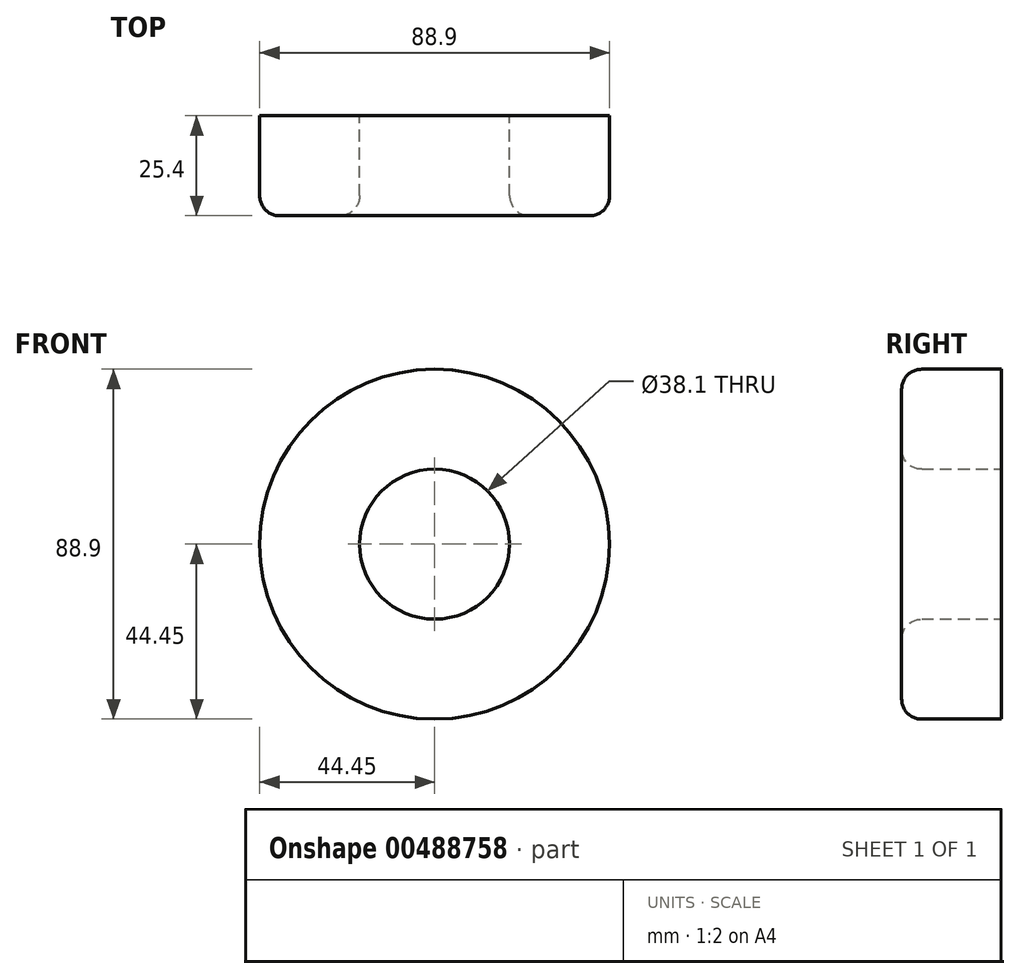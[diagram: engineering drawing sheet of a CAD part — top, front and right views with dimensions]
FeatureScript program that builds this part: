
annotation { "Feature Type Name" : "Feature", "Feature Type Description" : "" }
export const myFeature = defineFeature(function(context is Context, id is Id, definition is map)
    precondition{}
    {
        {
            var Q0;
            Q0=qCreatedBy(makeId("Front.planeOp"),FACE);
            var sketch = newSketch(context, id + "F0", { "sketchPlane" : qUnion([Q0])});
            skCircle(sketch, "E0", {"center": v(0, 0) * mm, "radius": 19.05 * mm});
            skCircle(sketch, "E1", {"center": v(0, 0) * mm, "radius": 44.45 * mm});
            skSolve(sketch);
        }
        {
            var Q0;
            Q0 = qSketchRegion(id + "F0", true);
            extrude(context, id + "F1", {"entities" : qUnion([Q0]), "depth" : 25.4 * mm});
        }
        {
            var Q0;
            Q0=makeQuery(id+"F1.opExtrude","CAP_FACE",FACE,{"disambiguationData":[OSD([sQuery(id+"F0.wireOp",EDGE,"E0"),sQuery(id+"F0.wireOp",EDGE,"E1")])],"isStart":false});
            fillet(context, id + "F2", {"entities" : qUnion([Q0]), "radius" : 5.08 * mm, "tangentPropagation" : true, "allowEdgeOverflow" : false});
        }
    });
